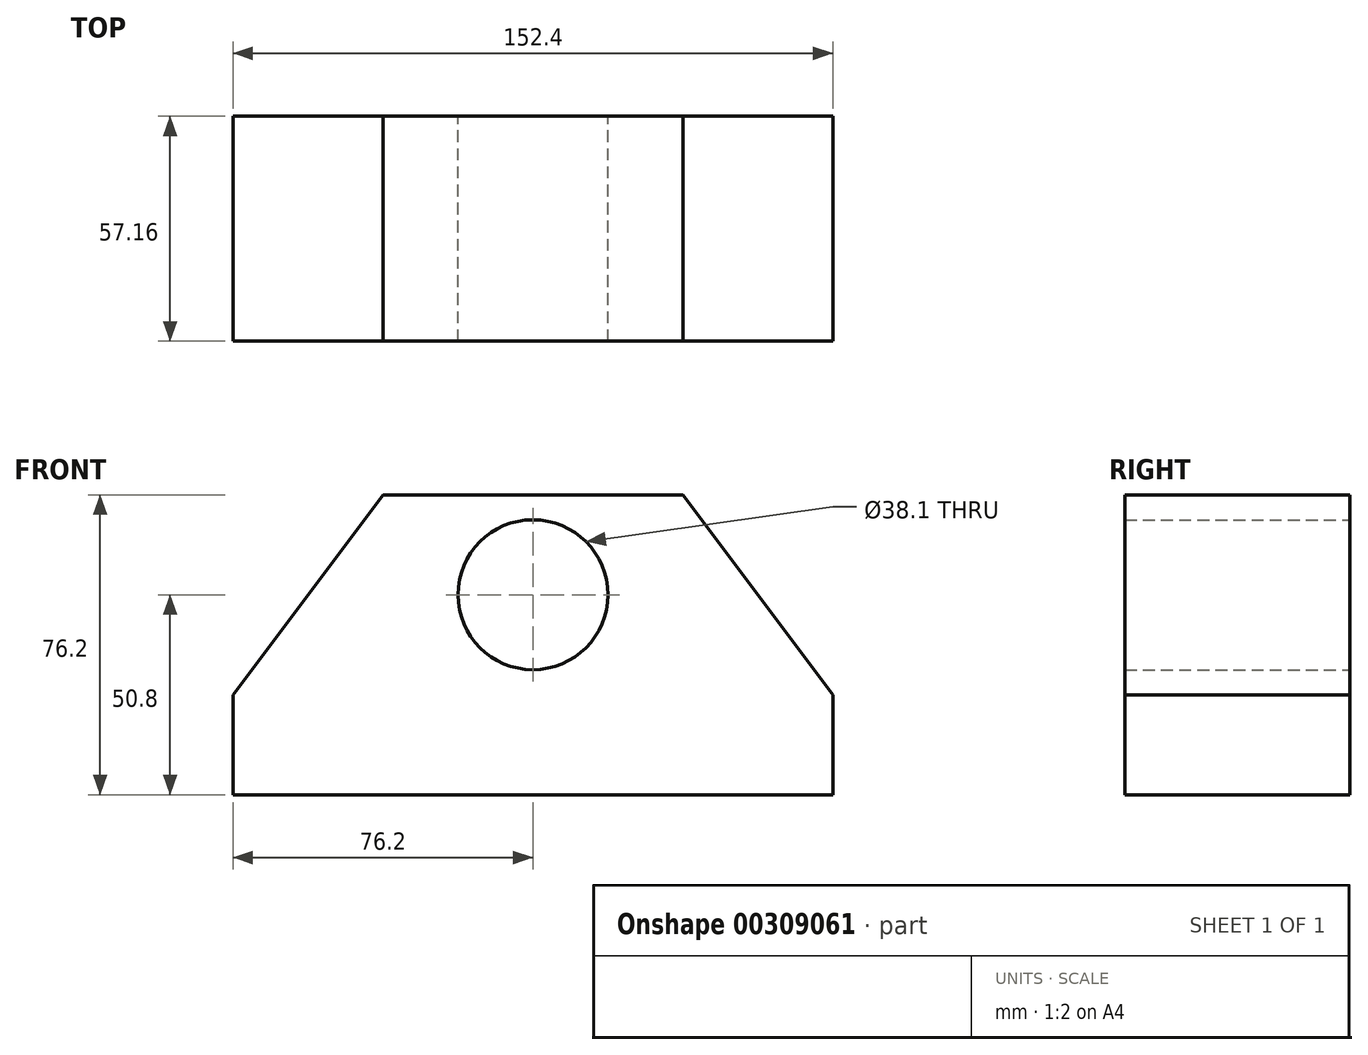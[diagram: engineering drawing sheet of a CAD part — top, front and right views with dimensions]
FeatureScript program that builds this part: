
annotation { "Feature Type Name" : "Feature", "Feature Type Description" : "" }
export const myFeature = defineFeature(function(context is Context, id is Id, definition is map)
    precondition{}
    {
        {
            var Q0;
            Q0=qCreatedBy(makeId("Front.planeOp"),FACE);
            var sketch = newSketch(context, id + "F0", { "sketchPlane" : qUnion([Q0])});
            skLineSegment(sketch, "E0", {"start": v(0, 0) * mm, "end": v(0, 25.4) * mm});
            skLineSegment(sketch, "E1", {"start": v(0, 25.4) * mm, "end": v(38.1, 76.2) * mm});
            skLineSegment(sketch, "E2", {"start": v(38.1, 76.2) * mm, "end": v(114.3, 76.2) * mm});
            skLineSegment(sketch, "E3", {"start": v(114.3, 76.2) * mm, "end": v(152.4, 25.4) * mm});
            skLineSegment(sketch, "E4", {"start": v(152.4, 25.4) * mm, "end": v(152.4, 0) * mm});
            skLineSegment(sketch, "E5", {"start": v(152.4, 0) * mm, "end": v(0, 0) * mm});
            skCircle(sketch, "E6", {"center": v(76.2, 50.8) * mm, "radius": 19.05 * mm});
            skPoint(sketch, "E6.centerSnap0", {"position": v(76.2, 76.2) * mm});
            skSolve(sketch);
        }
        {
            var Q0;
            Q0=makeQuery(id+"F0.imprint","IMPRINT",FACE,{"disambiguationData":[TD([[makeQuery(id+"F0.imprint","IMPRINT",EDGE,{"derivedFrom":sQuery(id+"F0.wireOp",EDGE,"E0")}),-1.0]])]});
            extrude(context, id + "F1", {"entities" : qUnion([Q0]), "depth" : 57.15 * mm, "symmetric" : true});
        }
    });
